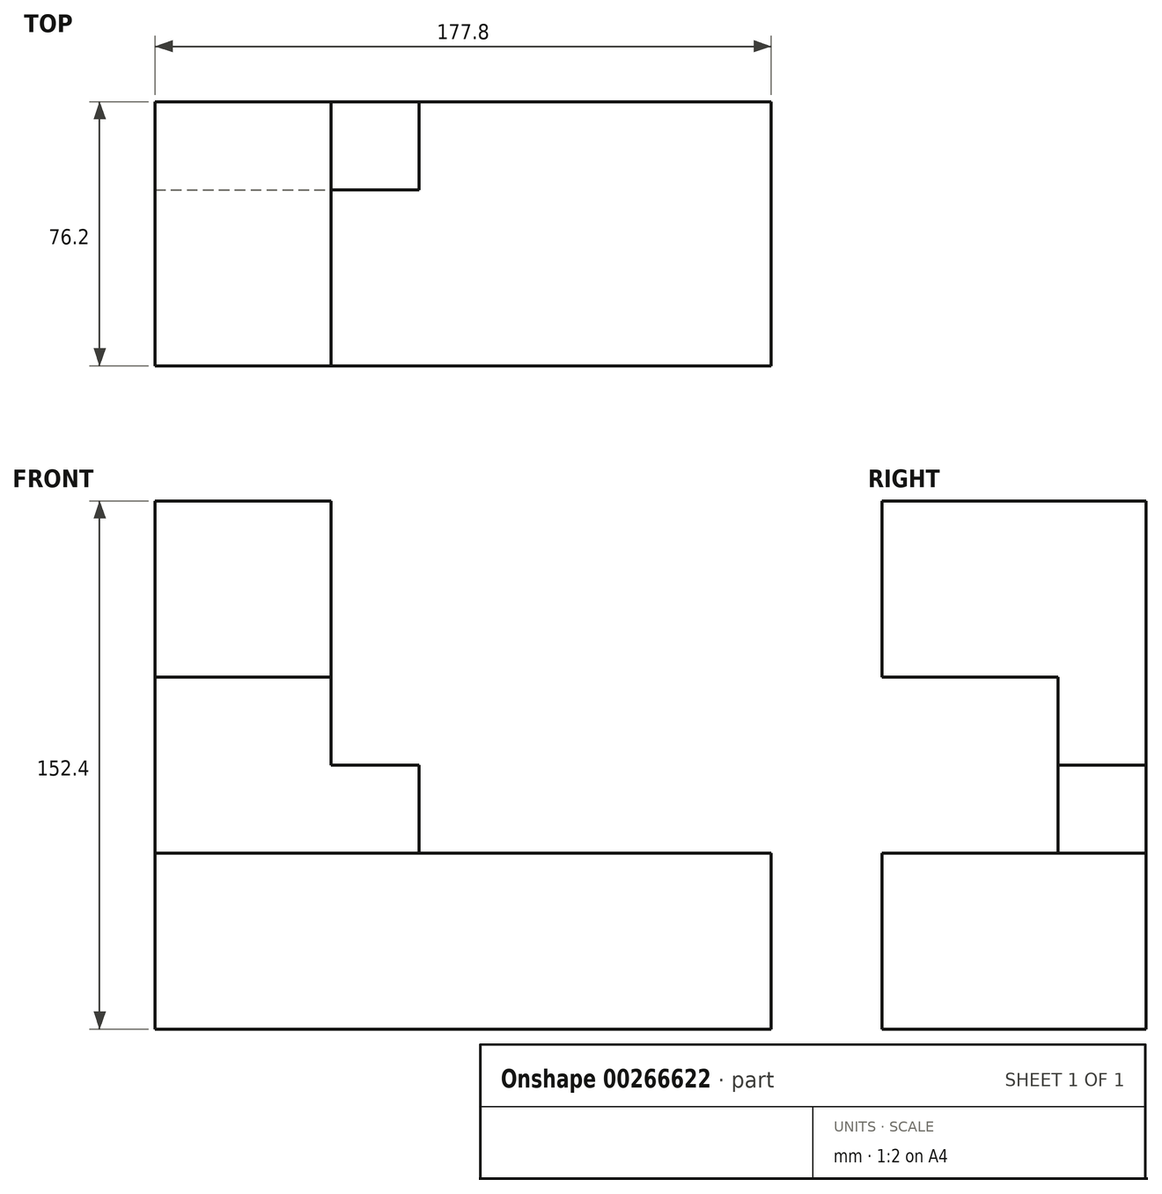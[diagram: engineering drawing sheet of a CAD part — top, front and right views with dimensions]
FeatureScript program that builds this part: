
annotation { "Feature Type Name" : "Feature", "Feature Type Description" : "" }
export const myFeature = defineFeature(function(context is Context, id is Id, definition is map)
    precondition{}
    {
        {
            var Q0;
            Q0=qCreatedBy(makeId("Top.planeOp"),FACE);
            var sketch = newSketch(context, id + "F0", { "sketchPlane" : qUnion([Q0])});
            skLineSegment(sketch, "E0.bottom", {"start": v(0, 0) * mm, "end": v(177.8, 0) * mm});
            skLineSegment(sketch, "E0.top", {"start": v(0, 76.2) * mm, "end": v(177.8, 76.2) * mm});
            skLineSegment(sketch, "E0.left", {"start": v(0, 0) * mm, "end": v(0, 76.2) * mm});
            skLineSegment(sketch, "E0.right", {"start": v(177.8, 0) * mm, "end": v(177.8, 76.2) * mm});
            skSolve(sketch);
        }
        {
            var Q0;
            Q0 = qSketchRegion(id + "F0", true);
            extrude(context, id + "F1", {"entities" : qUnion([Q0]), "depth" : 50.8 * mm});
        }
        {
            var Q0;
            Q0=makeQuery(id+"F1.opExtrude","CAP_FACE",FACE,{"disambiguationData":[OSD([sQuery(id+"F0.wireOp",EDGE,"E0.bottom"),sQuery(id+"F0.wireOp",EDGE,"E0.top"),sQuery(id+"F0.wireOp",EDGE,"E0.left"),sQuery(id+"F0.wireOp",EDGE,"E0.right")])],"isStart":false});
            var sketch = newSketch(context, id + "F2", { "sketchPlane" : qUnion([Q0])});
            skLineSegment(sketch, "E1.bottom", {"start": v(0, 76.2) * mm, "end": v(76.2, 76.2) * mm});
            skLineSegment(sketch, "E1.top", {"start": v(0, 50.8) * mm, "end": v(76.2, 50.8) * mm});
            skLineSegment(sketch, "E1.left", {"start": v(0, 76.2) * mm, "end": v(0, 50.8) * mm});
            skLineSegment(sketch, "E1.right", {"start": v(76.2, 76.2) * mm, "end": v(76.2, 50.8) * mm});
            skSolve(sketch);
        }
        {
            var Q0;
            Q0 = qSketchRegion(id + "F2", true);
            extrude(context, id + "F3", {"entities" : qUnion([Q0]), "operationType" : NewBodyOperationType.ADD, "depth" : 25.4 * mm});
        }
        {
            var Q0;
            Q0=makeQuery(id+"F3.opExtrude","CAP_FACE",FACE,{"disambiguationData":[OSD([sQuery(id+"F2.wireOp",EDGE,"E1.bottom"),sQuery(id+"F2.wireOp",EDGE,"E1.top"),sQuery(id+"F2.wireOp",EDGE,"E1.left"),sQuery(id+"F2.wireOp",EDGE,"E1.right")])],"isStart":false});
            var sketch = newSketch(context, id + "F4", { "sketchPlane" : qUnion([Q0])});
            skLineSegment(sketch, "E2.bottom", {"start": v(0, 76.2) * mm, "end": v(50.8, 76.2) * mm});
            skLineSegment(sketch, "E2.top", {"start": v(0, 50.8) * mm, "end": v(50.8, 50.8) * mm});
            skLineSegment(sketch, "E2.left", {"start": v(0, 76.2) * mm, "end": v(0, 50.8) * mm});
            skLineSegment(sketch, "E2.right", {"start": v(50.8, 76.2) * mm, "end": v(50.8, 50.8) * mm});
            skSolve(sketch);
        }
        {
            var Q0;
            Q0 = qSketchRegion(id + "F4", true);
            extrude(context, id + "F5", {"entities" : qUnion([Q0]), "operationType" : NewBodyOperationType.ADD, "depth" : 76.2 * mm});
        }
        {
            var Q0;
            Q0=makeQuery(id+"F5.boolean.opBoolean","MERGE",FACE,{"derivedFrom":[makeQuery(id+"F3.opExtrude","SWEPT_FACE",FACE,{"disambiguationData":[OSD([sQuery(id+"F2.wireOp",EDGE,"E1.top")])]}),makeQuery(id+"F5.opExtrude","SWEPT_FACE",FACE,{"disambiguationData":[OSD([sQuery(id+"F4.wireOp",EDGE,"E2.top")])]})]});
            var sketch = newSketch(context, id + "F6", { "sketchPlane" : qUnion([Q0])});
            skLineSegment(sketch, "E3.bottom", {"start": v(0, 152.4) * mm, "end": v(50.8, 152.4) * mm});
            skLineSegment(sketch, "E3.top", {"start": v(0, 101.6) * mm, "end": v(50.8, 101.6) * mm});
            skLineSegment(sketch, "E3.left", {"start": v(0, 152.4) * mm, "end": v(0, 101.6) * mm});
            skLineSegment(sketch, "E3.right", {"start": v(50.8, 152.4) * mm, "end": v(50.8, 101.6) * mm});
            skSolve(sketch);
        }
        {
            var Q0;
            Q0 = qSketchRegion(id + "F6", true);
            extrude(context, id + "F7", {"entities" : qUnion([Q0]), "operationType" : NewBodyOperationType.ADD, "depth" : 50.8 * mm});
        }
    });
